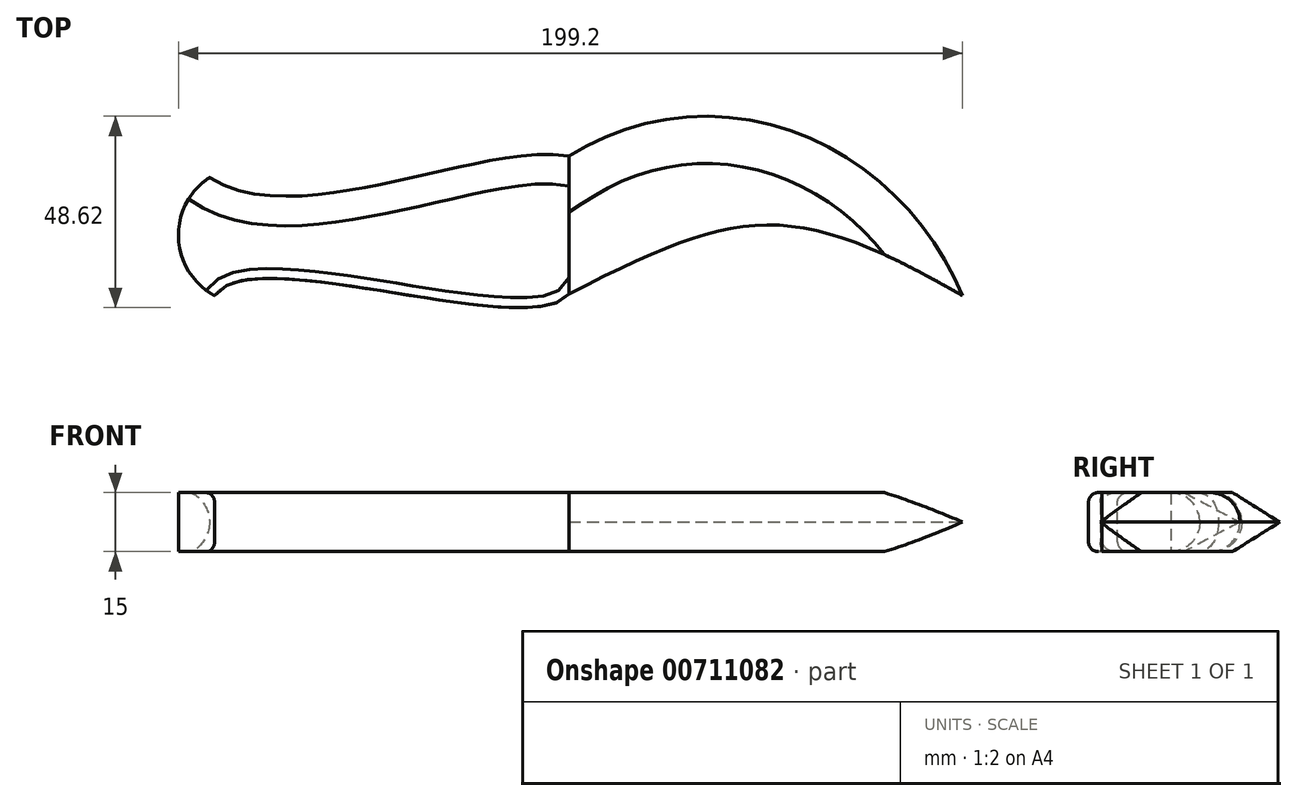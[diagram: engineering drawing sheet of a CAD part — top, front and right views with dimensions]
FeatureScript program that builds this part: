
annotation { "Feature Type Name" : "Feature", "Feature Type Description" : "" }
export const myFeature = defineFeature(function(context is Context, id is Id, definition is map)
    precondition{}
    {
        {
            var Q0;
            Q0=qCreatedBy(makeId("Top.planeOp"),FACE);
            var sketch = newSketch(context, id + "F0", { "sketchPlane" : qUnion([Q0])});
            skFitSpline(sketch, "E0", {"points": [v(100, 0) * mm, v(0, 0.44) * mm], "startDerivative": vector(-130.36, 75.1) * mm, "endDerivative": vector(-129.8, -66.78) * mm});
            skFitSpline(sketch, "E1", {"points": [v(100, 0) * mm, v(0, 35.44) * mm], "startDerivative": vector(-50.27, 120.34) * mm, "endDerivative": vector(-111.7, -69.52) * mm});
            skLineSegment(sketch, "E2", {"start": v(0, 35.44) * mm, "end": v(0, 0) * mm});
            skFitSpline(sketch, "E3", {"points": [v(0, 35.44) * mm, v(-91.32, 30) * mm], "startDerivative": vector(-63.86, 12.47) * mm, "endDerivative": vector(-66.88, 43.82) * mm});
            skFitSpline(sketch, "E4", {"points": [v(0, 0.44) * mm, v(-90, 0) * mm], "startDerivative": vector(-28.48, -37.42) * mm, "endDerivative": vector(-24.83, -42.75) * mm});
            skArc(sketch, "E5", {"start": v(-91.32, 30) * mm, "mid": v(-99.18, 14.63) * mm, "end": v(-90, 0) * mm});
            skSolve(sketch);
        }
        {
            var Q0;
            {var subQ2=sQuery(id+"F0.wireOp",EDGE,"E3");Q0=makeQuery(id+"F0.imprint","IMPRINT",FACE,{"disambiguationData":[TD([[makeQuery(id+"F0.imprint","IMPRINT",EDGE,{"derivedFrom":subQ2}),1.0]])]});}
            extrude(context, id + "F1", {"entities" : qUnion([Q0]), "endBound" : BoundingType.SYMMETRIC, "depth" : 15 * mm, "offsetDistance" : 25 * mm});
        }
        {
            var Q0;
            Q0=makeQuery(id+"F1.opExtrude","CAP_EDGE",EDGE,{"disambiguationData":[OSD([sQuery(id+"F0.wireOp",EDGE,"E3")])],"isStart":false});
            var Q1;
            Q1=makeQuery(id+"F1.opExtrude","CAP_EDGE",EDGE,{"disambiguationData":[OSD([sQuery(id+"F0.wireOp",EDGE,"E3")])],"isStart":true});
            fillet(context, id + "F2", {"entities" : qUnion([Q0, Q1]), "radius" : 7.5 * mm, "tangentPropagation" : true, "allowEdgeOverflow" : false});
        }
        {
            var Q0;
            Q0=makeQuery(id+"F1.opExtrude","CAP_EDGE",EDGE,{"disambiguationData":[OSD([sQuery(id+"F0.wireOp",EDGE,"E4")])],"isStart":false});
            var Q1;
            Q1=makeQuery(id+"F1.opExtrude","CAP_EDGE",EDGE,{"disambiguationData":[OSD([sQuery(id+"F0.wireOp",EDGE,"E4")])],"isStart":true});
            fillet(context, id + "F3", {"entities" : qUnion([Q0, Q1]), "radius" : 2.5 * mm, "tangentPropagation" : true, "allowEdgeOverflow" : false});
        }
        {
            var Q0;
            {var subQ0=sQuery(id+"F0.wireOp",EDGE,"E0");Q0=makeQuery(id+"F0.imprint","IMPRINT",FACE,{"disambiguationData":[TD([[makeQuery(id+"F0.imprint","IMPRINT",EDGE,{"derivedFrom":subQ0}),-1.0]])]});}
            extrude(context, id + "F4", {"entities" : qUnion([Q0]), "endBound" : BoundingType.SYMMETRIC, "depth" : 15 * mm, "offsetDistance" : 25 * mm});
        }
        {
            var Q0;
            Q0=makeQuery(id+"F4.opExtrude","CAP_EDGE",EDGE,{"disambiguationData":[OSD([sQuery(id+"F0.wireOp",EDGE,"E1")])],"isStart":true});
            var Q1;
            Q1=makeQuery(id+"F4.opExtrude","CAP_EDGE",EDGE,{"disambiguationData":[OSD([sQuery(id+"F0.wireOp",EDGE,"E1")])],"isStart":false});
            chamfer(context, id + "F5", {"entities" : qUnion([Q0, Q1]), "chamferType" : ChamferType.TWO_OFFSETS, "width1" : 7.5 * mm, "oppositeDirection" : false, "width2" : 12 * mm, "tangentPropagation" : true});
        }
    });
